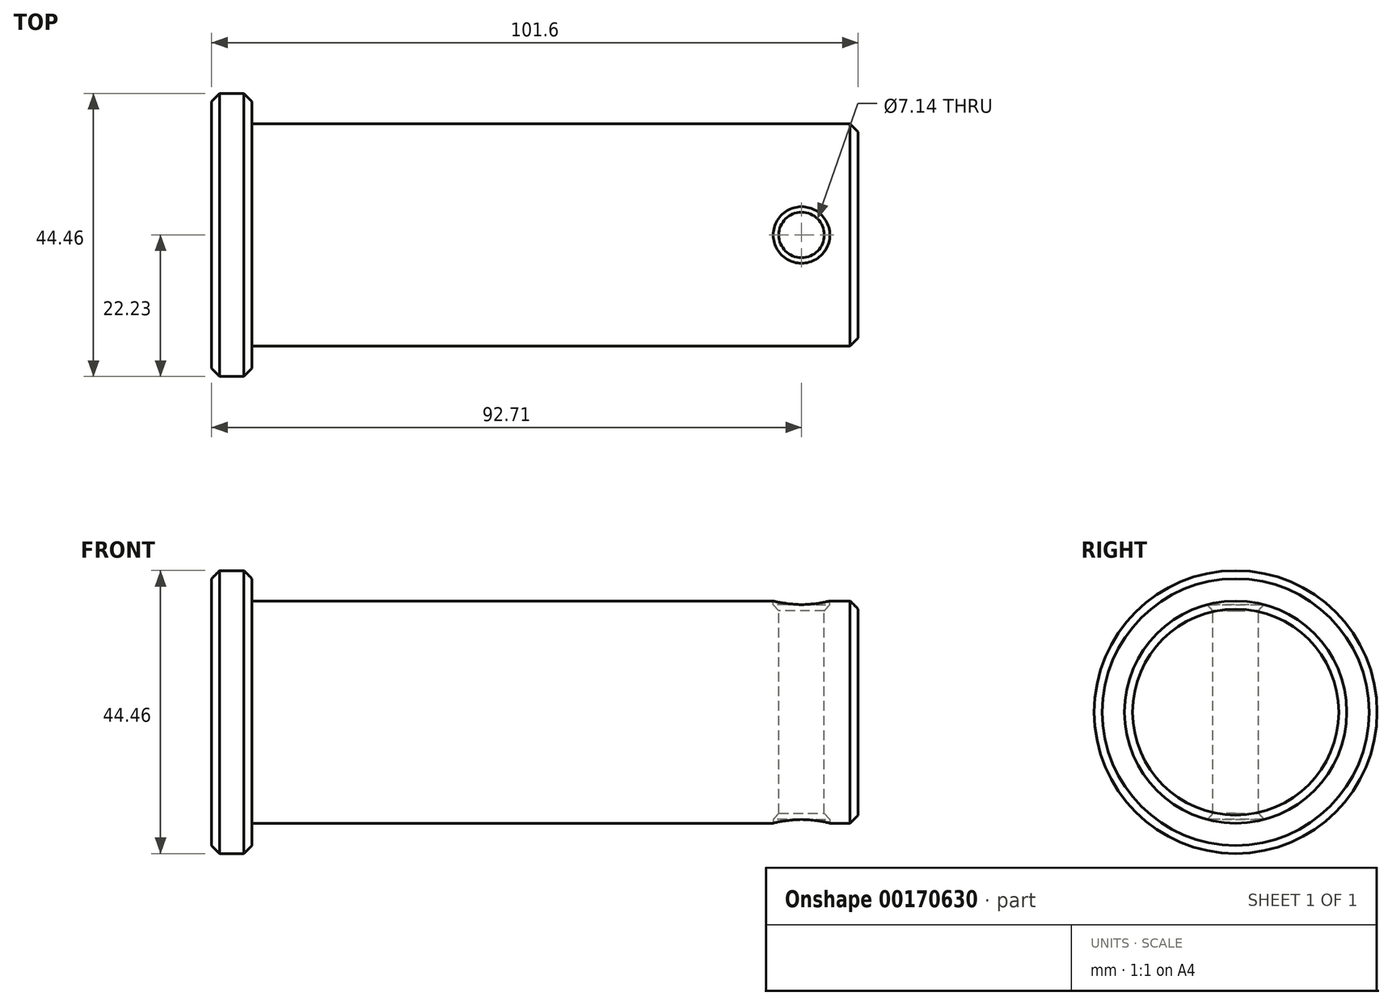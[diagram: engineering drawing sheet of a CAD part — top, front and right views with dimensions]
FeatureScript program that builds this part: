
annotation { "Feature Type Name" : "Feature", "Feature Type Description" : "" }
export const myFeature = defineFeature(function(context is Context, id is Id, definition is map)
    precondition{}
    {
        {
            var Q0;
            Q0=qCreatedBy(makeId("Front.planeOp"),FACE);
            var sketch = newSketch(context, id + "F0", { "sketchPlane" : qUnion([Q0])});
            skLineSegment(sketch, "E0", {"start": v(0, 0) * mm, "end": v(0, 16.2) * mm});
            skLineSegment(sketch, "E1", {"start": v(0, 16.2) * mm, "end": v(-1.27, 17.46) * mm});
            skLineSegment(sketch, "E2", {"start": v(-1.27, 17.46) * mm, "end": v(-95.25, 17.46) * mm});
            skLineSegment(sketch, "E3", {"start": v(-95.25, 17.46) * mm, "end": v(-95.25, 20.96) * mm});
            skLineSegment(sketch, "E4", {"start": v(-95.25, 20.96) * mm, "end": v(-96.52, 22.22) * mm});
            skLineSegment(sketch, "E5", {"start": v(-96.52, 22.23) * mm, "end": v(-100.33, 22.23) * mm});
            skLineSegment(sketch, "E6", {"start": v(-100.33, 22.22) * mm, "end": v(-101.6, 20.95) * mm});
            skLineSegment(sketch, "E7", {"start": v(-101.6, 20.95) * mm, "end": v(-101.6, 0) * mm});
            skLineSegment(sketch, "E8", {"start": v(-101.6, 0) * mm, "end": v(0, 0) * mm});
            skLineSegment(sketch, "E9", {"start": v(-116.35, 0) * mm, "end": v(14.22, 0) * mm, "construction": true});
            skSolve(sketch);
        }
        {
            var Q0;
            Q0=makeQuery(id+"F0.imprint","IMPRINT",FACE,{"disambiguationData":[TD([[makeQuery(id+"F0.imprint","IMPRINT",EDGE,{"derivedFrom":sQuery(id+"F0.wireOp",EDGE,"E0")}),1.0]])]});
            var Q1;
            Q1=sQuery(id+"F0.wireOp",EDGE,"E9");
            revolve(context, id + "F1", {"entities" : qUnion([Q0]), "axis" : qUnion([Q1]), "revolveType" : RevolveType.FULL});
        }
        {
            var Q0;
            Q0=qCreatedBy(makeId("Top.planeOp"),FACE);
            cPlane(context, id + "F2", {"entities" : qUnion([Q0]), "cplaneType" : CPlaneType.OFFSET, "offset" : 17.46 * mm, "width" : 152.4 * mm, "height" : 152.4 * mm});
        }
        {
            var Q0;
            Q0=qCreatedBy(id+"F2.planeOp",FACE);
            var sketch = newSketch(context, id + "F3", { "sketchPlane" : qUnion([Q0])});
            skCircle(sketch, "E10", {"center": v(-8.9, 0) * mm, "radius": 3.56 * mm});
            skSolve(sketch);
        }
        {
            var Q0;
            Q0=sQuery(id+"F3.wireOp",VERTEX,"E10.center");
            var Q1;
            Q1=makeQuery(id+"F1.opRevolve","SWEPT_BODY",BODY,{"disambiguationData":[OSD([sQuery(id+"F0.wireOp",EDGE,"E0"),sQuery(id+"F0.wireOp",EDGE,"E1"),sQuery(id+"F0.wireOp",EDGE,"E2"),sQuery(id+"F0.wireOp",EDGE,"E3"),sQuery(id+"F0.wireOp",EDGE,"E4"),sQuery(id+"F0.wireOp",EDGE,"E5"),sQuery(id+"F0.wireOp",EDGE,"E6"),sQuery(id+"F0.wireOp",EDGE,"E7"),sQuery(id+"F0.wireOp",EDGE,"E8")])]});
            hole(context, id + "F4", {"style" : HoleStyle.C_SINK, "endStyle" : HoleEndStyle.THROUGH, "standardTappedOrClearance" : lookupTablePath({ "standard" : "ANSI", "size" : "K (0.28)", "type" : "Drilled" }), "standardBlindInLast" : lookupTablePath({ "standard" : "ANSI", "size" : "K", "type" : "Drilled" }), "holeDiameter" : 7.14 * mm, "cSinkDiameter" : 8.9 * mm, "cSinkAngle" : 82 * degree, "locations" : qUnion([Q0]), "scope" : qUnion([Q1]), "isTappedThrough" : true});
        }
        {
            var Q0;
            Q0=qCreatedBy(makeId("Top.planeOp"),FACE);
            cPlane(context, id + "F5", {"entities" : qUnion([Q0]), "cplaneType" : CPlaneType.OFFSET, "offset" : 17.48 * mm, "oppositeDirection" : true, "width" : 152.4 * mm, "height" : 152.4 * mm});
        }
        {
            var Q0;
            Q0=qCreatedBy(id+"F5.planeOp",FACE);
            var sketch = newSketch(context, id + "F6", { "sketchPlane" : qUnion([Q0])});
            skCircle(sketch, "E11", {"center": v(-8.9, 0) * mm, "radius": 3.56 * mm});
            skSolve(sketch);
        }
        {
            var Q0;
            Q0=sQuery(id+"F6.wireOp",VERTEX,"E11.center");
            var Q1;
            Q1=makeQuery(id+"F1.opRevolve","SWEPT_BODY",BODY,{"disambiguationData":[OSD([sQuery(id+"F0.wireOp",EDGE,"E0"),sQuery(id+"F0.wireOp",EDGE,"E1"),sQuery(id+"F0.wireOp",EDGE,"E2"),sQuery(id+"F0.wireOp",EDGE,"E3"),sQuery(id+"F0.wireOp",EDGE,"E4"),sQuery(id+"F0.wireOp",EDGE,"E5"),sQuery(id+"F0.wireOp",EDGE,"E6"),sQuery(id+"F0.wireOp",EDGE,"E7"),sQuery(id+"F0.wireOp",EDGE,"E8")])]});
            hole(context, id + "F7", {"style" : HoleStyle.C_SINK, "endStyle" : HoleEndStyle.THROUGH, "oppositeDirection" : true, "standardTappedOrClearance" : lookupTablePath({ "standard" : "ANSI", "size" : "K (0.28)", "type" : "Drilled" }), "standardBlindInLast" : lookupTablePath({ "standard" : "ANSI", "size" : "K", "type" : "Drilled" }), "holeDiameter" : 7.14 * mm, "cSinkDiameter" : 8.9 * mm, "cSinkAngle" : 82 * degree, "locations" : qUnion([Q0]), "scope" : qUnion([Q1]), "isTappedThrough" : true});
        }
    });
